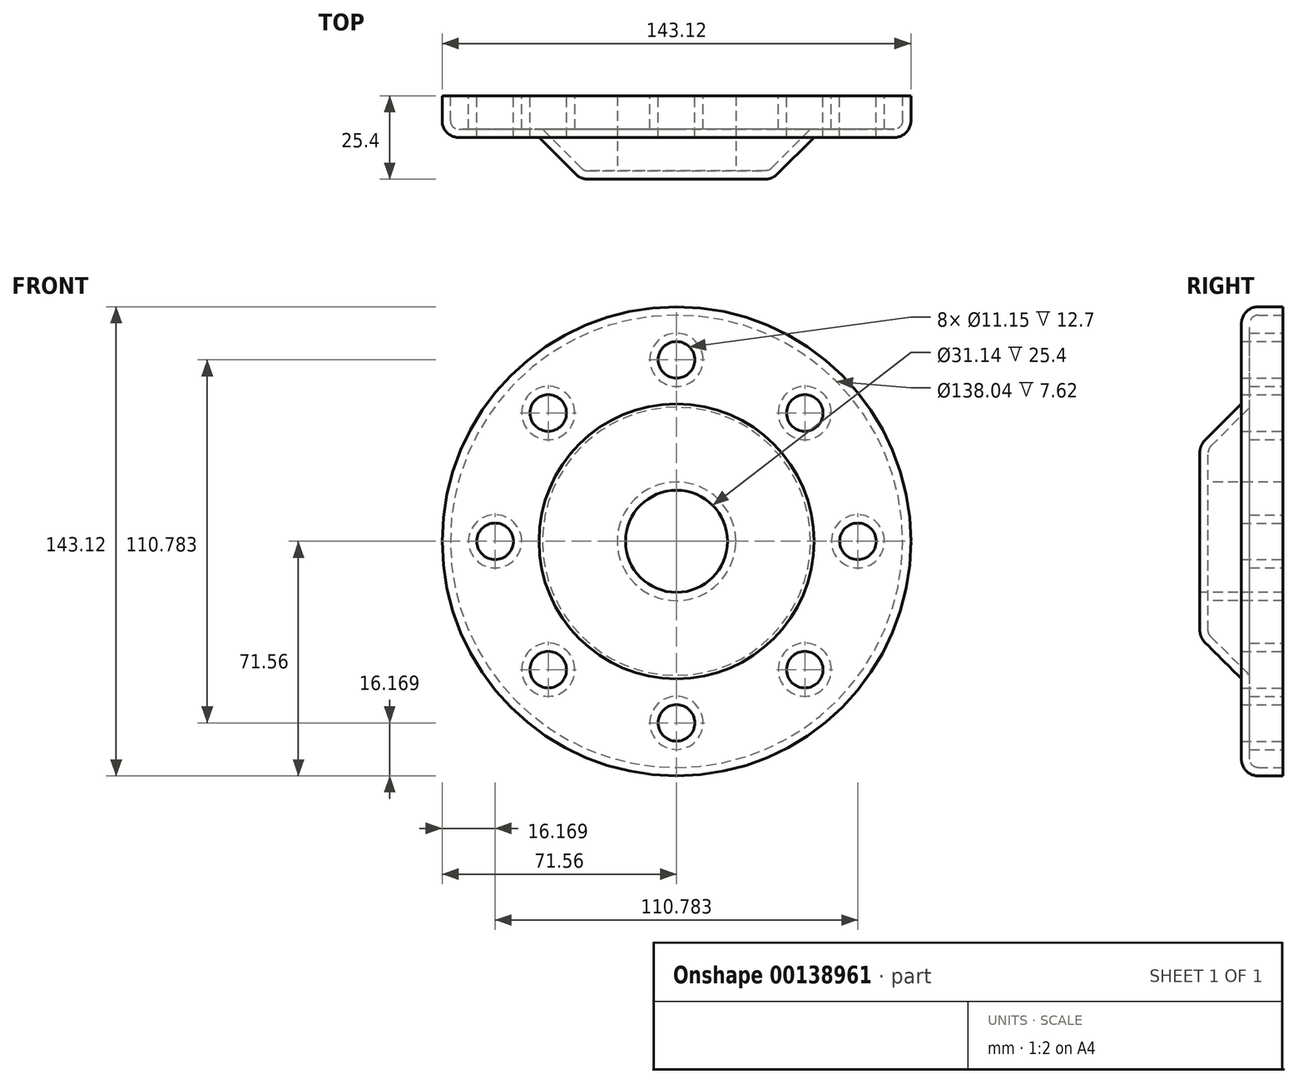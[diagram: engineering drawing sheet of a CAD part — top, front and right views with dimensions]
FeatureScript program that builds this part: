
annotation { "Feature Type Name" : "Feature", "Feature Type Description" : "" }
export const myFeature = defineFeature(function(context is Context, id is Id, definition is map)
    precondition{}
    {
        {
            var Q0;
            Q0=qCreatedBy(makeId("Front.planeOp"),FACE);
            var sketch = newSketch(context, id + "F0", { "sketchPlane" : qUnion([Q0])});
            skCircle(sketch, "E0", {"center": v(0, 0) * mm, "radius": 71.56 * mm});
            skSolve(sketch);
        }
        {
            var Q0;
            Q0 = qSketchRegion(id + "F0", true);
            extrude(context, id + "F1", {"entities" : qUnion([Q0]), "depth" : 12.7 * mm});
        }
        {
            var Q0;
            Q0=qCreatedBy(makeId("Front.planeOp"),FACE);
            cPlane(context, id + "F2", {"entities" : qUnion([Q0]), "cplaneType" : CPlaneType.OFFSET, "offset" : 12.7 * mm, "width" : 152.4 * mm, "height" : 152.4 * mm});
        }
        {
            var Q0;
            Q0=qCreatedBy(id+"F2.planeOp",FACE);
            var sketch = newSketch(context, id + "F3", { "sketchPlane" : qUnion([Q0])});
            skCircle(sketch, "E1", {"center": v(0, 0) * mm, "radius": 41.97 * mm});
            skSolve(sketch);
        }
        {
            var Q0;
            Q0 = qSketchRegion(id + "F3", true);
            extrude(context, id + "F4", {"entities" : qUnion([Q0]), "operationType" : NewBodyOperationType.ADD, "depth" : 12.7 * mm, "hasDraft" : true, "draftAngle" : 45 * degree, "draftPullDirection" : true});
        }
        {
            var Q0;
            Q0=qCreatedBy(id+"F2.planeOp",FACE);
            var sketch = newSketch(context, id + "F5", { "sketchPlane" : qUnion([Q0])});
            skCircle(sketch, "E2", {"center": v(0, 0) * mm, "radius": 15.57 * mm});
            skSolve(sketch);
        }
        {
            var Q0;
            Q0 = qSketchRegion(id + "F5", true);
            extrude(context, id + "F6", {"entities" : qUnion([Q0]), "operationType" : NewBodyOperationType.REMOVE, "oppositeDirection" : true, "depth" : 25.4 * mm, "hasSecondDirection" : true, "secondDirectionOppositeDirection" : false, "secondDirectionDepth" : 25.4 * mm});
        }
        {
            var Q0;
            Q0=qCreatedBy(makeId("Front.planeOp"),FACE);
            var sketch = newSketch(context, id + "F7", { "sketchPlane" : qUnion([Q0])});
            skCircle(sketch, "E3", {"center": v(0, 55.4) * mm, "radius": 5.58 * mm});
            skCircle(sketch, "E4.1.0", {"center": v(-39.17, 39.17) * mm, "radius": 5.58 * mm});
            skCircle(sketch, "E4.2.0", {"center": v(-55.4, 0) * mm, "radius": 5.58 * mm});
            skCircle(sketch, "E4.3.0", {"center": v(-39.17, -39.17) * mm, "radius": 5.58 * mm});
            skCircle(sketch, "E4.4.0", {"center": v(0, -55.4) * mm, "radius": 5.58 * mm});
            skCircle(sketch, "E4.5.0", {"center": v(39.17, -39.17) * mm, "radius": 5.58 * mm});
            skCircle(sketch, "E4.6.0", {"center": v(55.4, 0) * mm, "radius": 5.58 * mm});
            skCircle(sketch, "E4.7.0", {"center": v(39.17, 39.17) * mm, "radius": 5.58 * mm});
            skPoint(sketch, "E4.center", {"position": v(0, 0) * mm});
            skSolve(sketch);
        }
        {
            var Q0;
            Q0 = qSketchRegion(id + "F7", true);
            extrude(context, id + "F8", {"entities" : qUnion([Q0]), "operationType" : NewBodyOperationType.REMOVE, "depth" : 25.4 * mm});
        }
        {
            var Q0;
            Q0=makeQuery(id+"F1.opExtrude","CAP_EDGE",EDGE,{"disambiguationData":[OSD([sQuery(id+"F0.wireOp",EDGE,"E0")])],"isStart":false});
            var Q1;
            Q1=makeQuery(id+"F4.opExtrude","CAP_EDGE",EDGE,{"disambiguationData":[OSD([sQuery(id+"F3.wireOp",EDGE,"E1")])],"isStart":true});
            var Q2;
            Q2=makeQuery(id+"F4.opExtrude","CAP_EDGE",EDGE,{"disambiguationData":[OSD([sQuery(id+"F3.wireOp",EDGE,"E1")])],"isStart":false});
            fillet(context, id + "F9", {"entities" : qUnion([Q0, Q1, Q2]), "radius" : 5.08 * mm, "tangentPropagation" : true, "allowEdgeOverflow" : false});
        }
        {
            var Q0;
            Q0=makeQuery(id+"F1.opExtrude","CAP_FACE",FACE,{"disambiguationData":[OSD([sQuery(id+"F0.wireOp",EDGE,"E0")])],"isStart":true});
            shell(context, id + "F10", {"entities" : qUnion([Q0]), "thickness" : 2.54 * mm});
        }
    });
